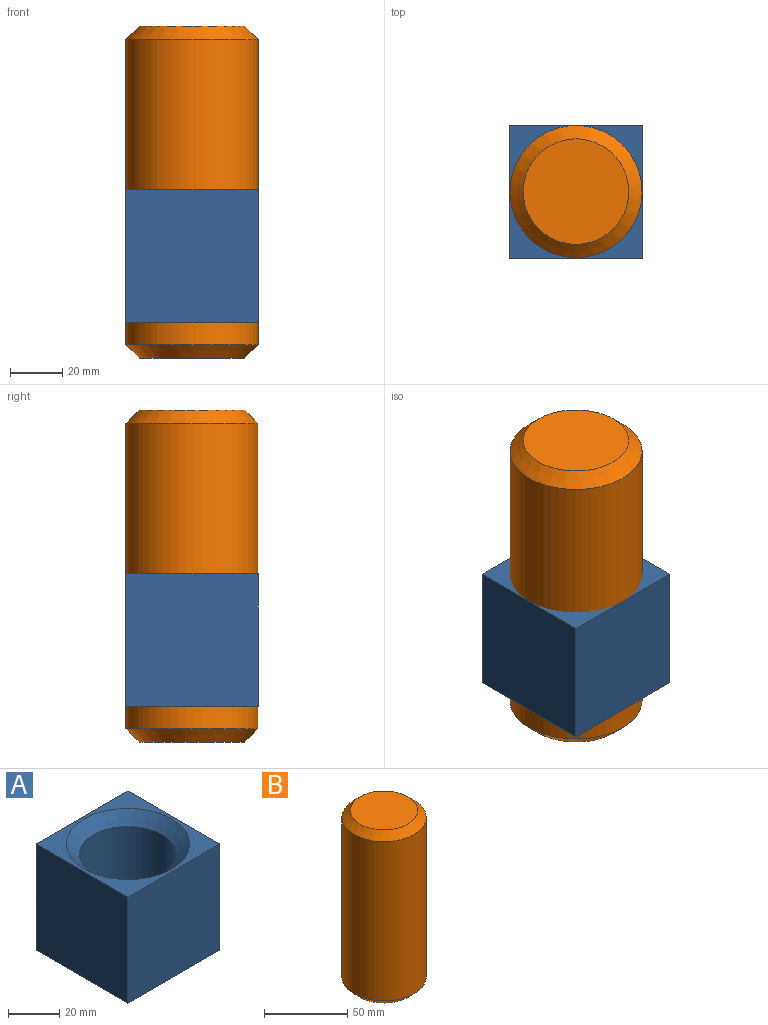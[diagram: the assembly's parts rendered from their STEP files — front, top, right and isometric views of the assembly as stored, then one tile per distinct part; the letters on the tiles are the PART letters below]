
ASSEMBLY  parts=2 mates=1
PART A: 9 faces, bbox 50.8x50.8x50.8 mm
  f0: plane 50.8x50.8mm, normal (-1,0,0), area 2580.6mm2, adj f1,f3,f4,f5
  f1: plane 50.8x50.8mm, normal (0,-1,0), area 2580.6mm2, adj f0,f2,f4,f5
  f2: plane 50.8x50.8mm, normal (1,0,0), area 2580.6mm2, adj f1,f3,f4,f5
  f3: plane 50.8x50.8mm, normal (0,1,0), area 2580.6mm2, adj f0,f2,f4,f5
  f4: plane 50.8x50.8mm, normal (0,0,1), area 751.4mm2, adj f0,f1,f2,f3,f7
  f5: plane 50.8x50.8mm, normal (0,0,-1), area 751.4mm2, adj f0,f1,f2,f3,f8
  f6: cylinder r=19.05mm len=40.64mm, axis (0,0,1), area 4864.4mm2, adj f7,f8
  f7: cone r=19.05mm half-angle=45deg, axis (0,0,1), area 974.6mm2, adj f4,f6
  f8: cone r=24.13mm half-angle=45deg, axis (0,0,-1), area 974.6mm2, adj f5,f6
PART B: 5 faces, bbox 50.5x50.5x127 mm
  f0: cylinder r=25.27mm len=116.84mm, axis (0,0,-1), area 18553.6mm2, adj f3,f4
  f1: plane 40.39x40.39mm, normal (0,0,1), area 1281mm2, adj f4
  f2: plane 40.39x40.39mm, normal (0,0,-1), area 1281mm2, adj f3
  f3: cone r=25.27mm half-angle=45deg, axis (0,0,1), area 1026.2mm2, adj f0,f2
  f4: cone r=20.19mm half-angle=45deg, axis (0,0,-1), area 1026.2mm2, adj f0,f1
PLACE A rot(axis=(0.71,0.71,0),180deg) t=(-17.09,164.8,-151.39)mm
PLACE B rot(axis=(0,0,1),90deg) t=(47.79,248.51,-215.73)mm
MATE slider B.f0 <-> A.f6  axis (0,0,1) through (8.31,190.2,-88.73)mm
